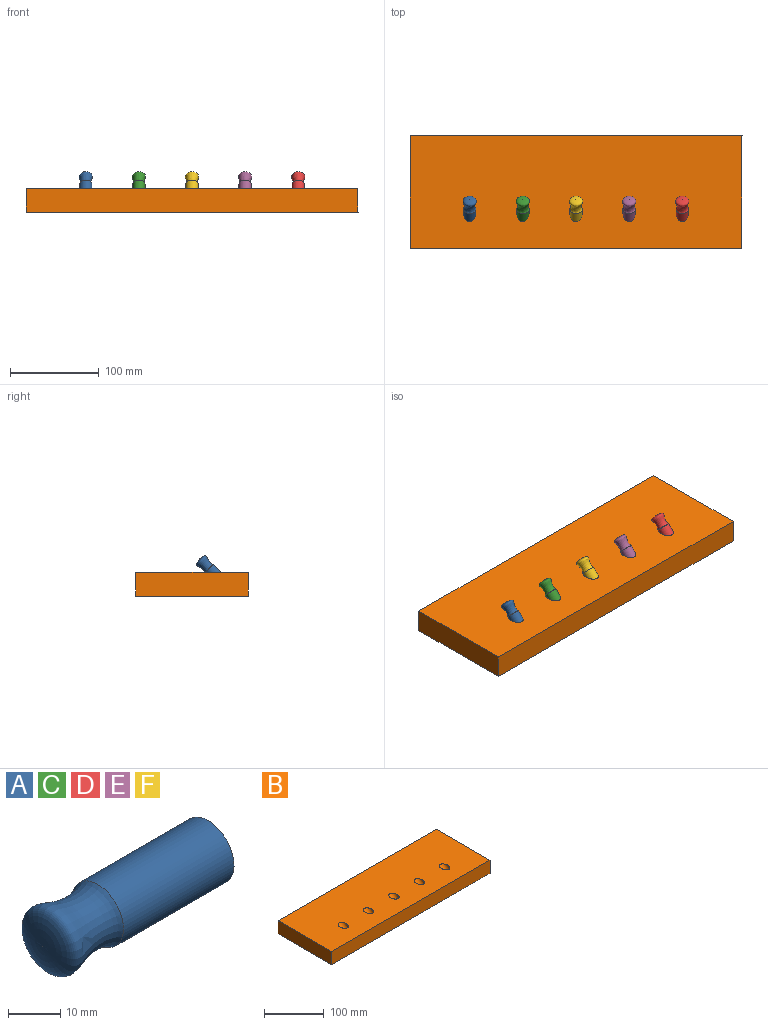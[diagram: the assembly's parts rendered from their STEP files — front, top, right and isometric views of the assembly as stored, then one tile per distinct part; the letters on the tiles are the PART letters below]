
ASSEMBLY  parts=6 mates=1
PART A: 3 faces, bbox 45x15x15 mm
  f0: revolved ~15.02x15.02mm, area 742.3mm2, adj f2
  f1: plane 14x14mm, normal (1,0,0), area 153.9mm2, adj f2
  f2: cylinder r=7mm len=30mm, axis (-1,0,0), area 1319.5mm2, adj f0,f1
PART B: 11 faces, bbox 375x127x46.9 mm
  f0: plane 375x27mm, normal (0,1,0), area 10125mm2, adj f1,f3,f4,f5
  f1: plane 127x27mm, normal (-1,0,0), area 3429mm2, adj f0,f2,f4,f5
  f2: plane 375x27mm, normal (0,-1,0), area 10125mm2, adj f1,f3,f4,f5
  f3: plane 127x27mm, normal (1,0,0), area 3429mm2, adj f0,f2,f4,f5
  f4: plane 375x127mm, normal (0,0,1), area 46536.5mm2, adj f0,f1,f2,f3,f6,f7,f8,f9
  f5: plane 375x127mm, normal (0,0,-1), area 46536.5mm2, adj f0,f1,f2,f3,f6,f7,f8,f9
  f6: cylinder r=7mm len=46.87mm, axis (0,0.71,0.71), area 1679.4mm2, adj f4,f5
  f7: cylinder r=7mm len=46.87mm, axis (0,0.71,0.71), area 1679.4mm2, adj f4,f5
  f8: cylinder r=7mm len=46.87mm, axis (0,0.71,0.71), area 1679.4mm2, adj f4,f5
  f9: cylinder r=7mm len=46.87mm, axis (0,0.71,0.71), area 1679.4mm2, adj f4,f5
  f10: cylinder r=7mm len=46.87mm, axis (0,0.71,0.71), area 1679.4mm2, adj f4,f5
PART C: same geometry as A
PART D: same geometry as A
PART E: same geometry as A
PART F: same geometry as A
PLACE A rot(axis=(-0.36,0.86,-0.36),98.4deg) t=(78.48,-60.16,186.09)mm
PLACE B t=(198.48,-51.44,144.3)mm
PLACE C rot(axis=(-0.36,0.86,-0.36),98.4deg) t=(138.48,-60.16,186.09)mm
PLACE D rot(axis=(-0.36,0.86,-0.36),98.4deg) t=(318.48,-60.16,186.09)mm
PLACE E rot(axis=(-0.36,0.86,-0.36),98.4deg) t=(258.48,-60.16,186.09)mm
PLACE F rot(axis=(-0.36,0.86,-0.36),98.4deg) t=(198.48,-60.16,186.09)mm
MATE slider D.f2 <-> B.f10  axis (0,0.71,0.71) through (318.48,-91.98,154.27)mm
